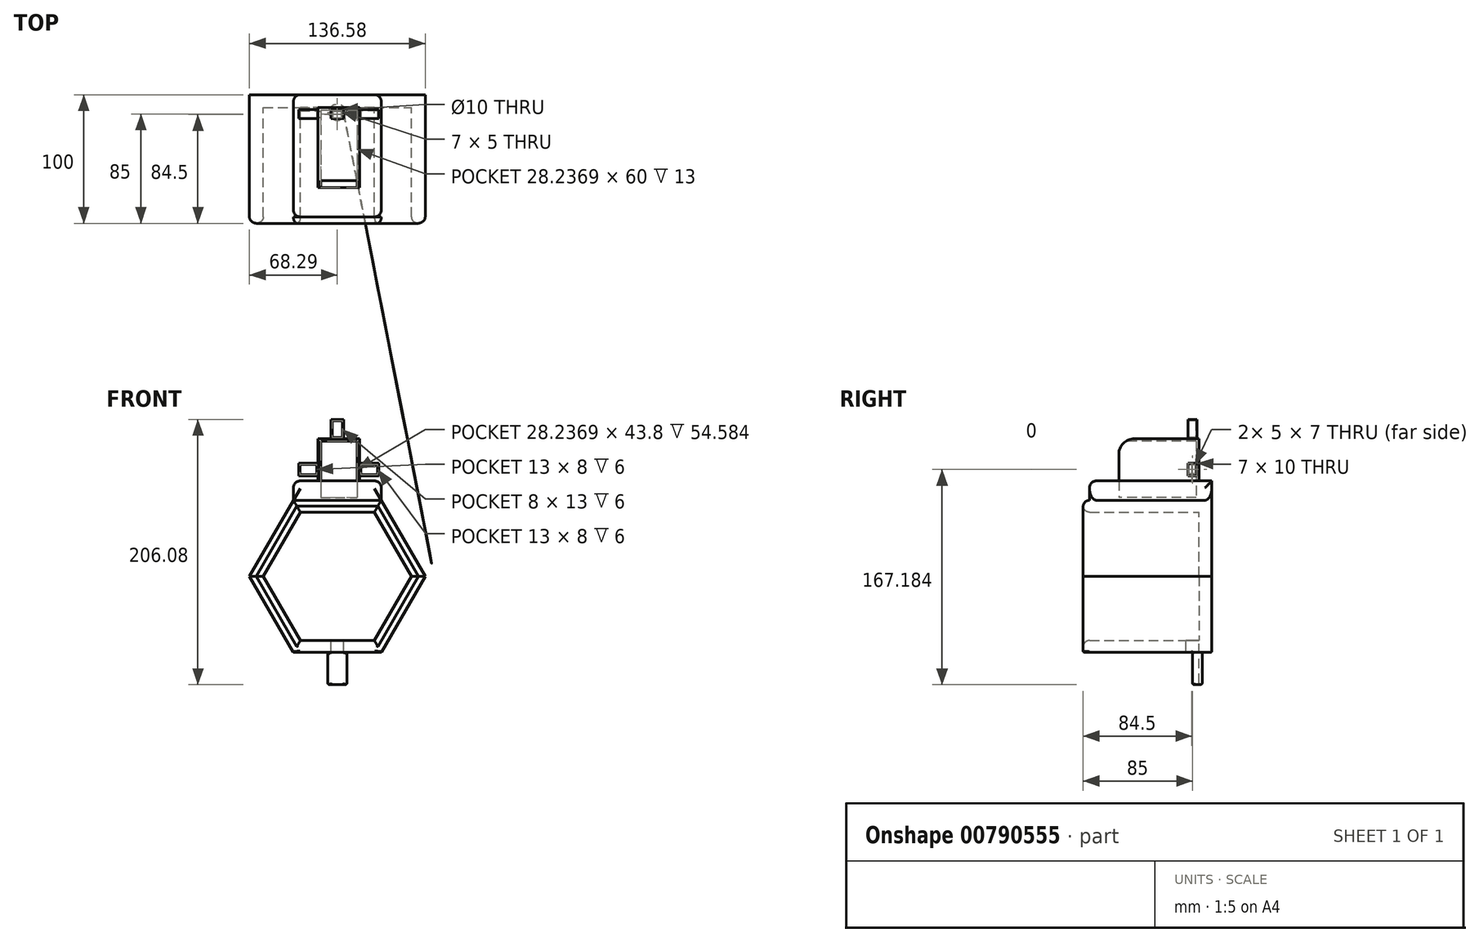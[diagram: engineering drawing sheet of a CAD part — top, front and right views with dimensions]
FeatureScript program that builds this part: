
annotation { "Feature Type Name" : "Feature", "Feature Type Description" : "" }
export const myFeature = defineFeature(function(context is Context, id is Id, definition is map)
    precondition{}
    {
        {
            var Q0;
            Q0=qCreatedBy(makeId("Front.planeOp"),FACE);
            var sketch = newSketch(context, id + "F0", { "sketchPlane" : qUnion([Q0])});
            skLineSegment(sketch, "E0.0", {"start": v(-34.15, 59.14) * mm, "end": v(34.15, 59.14) * mm});
            skLineSegment(sketch, "E0.1", {"start": v(34.15, 59.14) * mm, "end": v(68.3, 0) * mm});
            skLineSegment(sketch, "E0.2", {"start": v(68.3, 0) * mm, "end": v(34.15, -59.14) * mm});
            skLineSegment(sketch, "E0.3", {"start": v(34.15, -59.14) * mm, "end": v(-34.15, -59.14) * mm});
            skLineSegment(sketch, "E0.4", {"start": v(-34.15, -59.14) * mm, "end": v(-68.3, 0) * mm});
            skLineSegment(sketch, "E0.5", {"start": v(-68.3, 0) * mm, "end": v(-34.15, 59.14) * mm});
            skPoint(sketch, "E0.0.midPoint", {"position": v(0, 59.14) * mm});
            skLineSegment(sketch, "E1.0", {"start": v(-28.78, 49.85) * mm, "end": v(28.78, 49.85) * mm});
            skLineSegment(sketch, "E1.1", {"start": v(28.78, 49.85) * mm, "end": v(57.56, 0) * mm});
            skLineSegment(sketch, "E1.2", {"start": v(57.56, 0) * mm, "end": v(28.78, -49.85) * mm});
            skLineSegment(sketch, "E1.3", {"start": v(28.78, -49.85) * mm, "end": v(-28.78, -49.85) * mm});
            skLineSegment(sketch, "E1.4", {"start": v(-28.78, -49.85) * mm, "end": v(-57.56, 0) * mm});
            skLineSegment(sketch, "E1.5", {"start": v(-57.56, 0) * mm, "end": v(-28.78, 49.85) * mm});
            skPoint(sketch, "E1.0.midPoint", {"position": v(0, 49.85) * mm});
            skPoint(sketch, "E1.cCircle.center.orphan", {"position": v(0, 0) * mm});
            skSolve(sketch);
        }
        {
            var Q0;
            Q0=makeQuery(id+"F0.imprint","IMPRINT",FACE,{"disambiguationData":[TD([[makeQuery(id+"F0.imprint","IMPRINT",EDGE,{"derivedFrom":sQuery(id+"F0.wireOp",EDGE,"E0.0")}),-1.0]])]});
            extrude(context, id + "F1", {"entities" : qUnion([Q0]), "depth" : 100 * mm, "offsetDistance" : 25 * mm});
        }
        {
            var Q0;
            Q0=makeQuery(id+"F0.imprint","IMPRINT",FACE,{"disambiguationData":[TD([[makeQuery(id+"F0.imprint","IMPRINT",EDGE,{"derivedFrom":sQuery(id+"F0.wireOp",EDGE,"E1.0")}),-1.0]])]});
            extrude(context, id + "F2", {"entities" : qUnion([Q0]), "operationType" : NewBodyOperationType.ADD, "depth" : 10 * mm, "offsetDistance" : 25 * mm});
        }
        {
            var Q0;
            Q0=makeQuery(id+"F1.opExtrude","SWEPT_FACE",FACE,{"disambiguationData":[OSD([sQuery(id+"F0.wireOp",EDGE,"E0.3")])]});
            var sketch = newSketch(context, id + "F3", { "sketchPlane" : qUnion([Q0])});
            skArc(sketch, "E2", {"start": v(-5, 15) * mm, "mid": v(0, 10) * mm, "end": v(5, 15) * mm});
            skPoint(sketch, "E3.start.orphan", {"position": v(0, 0) * mm});
            skArc(sketch, "E4", {"start": v(-7.5, 15) * mm, "mid": v(0, 7.5) * mm, "end": v(7.5, 15) * mm});
            skPoint(sketch, "E5.orphan", {"position": v(0, 20) * mm});
            skPoint(sketch, "E6.end.orphan", {"position": v(0, 10) * mm});
            skLineSegment(sketch, "E7", {"start": v(-5, 15) * mm, "end": v(-7.5, 15) * mm});
            skLineSegment(sketch, "E8.trimOffspring", {"start": v(5, 15) * mm, "end": v(7.5, 15) * mm});
            skSolve(sketch);
        }
        {
            var Q0;
            Q0=makeQuery(id+"F3.imprint","IMPRINT",FACE,{"disambiguationData":[TD([[makeQuery(id+"F3.imprint","IMPRINT",EDGE,{"derivedFrom":sQuery(id+"F3.wireOp",EDGE,"E2")}),-1.0]])]});
            extrude(context, id + "F4", {"entities" : qUnion([Q0]), "operationType" : NewBodyOperationType.ADD, "depth" : 25 * mm, "offsetDistance" : 25 * mm});
        }
        {
            var Q0;
            Q0=makeQuery(id+"F1.opExtrude","SWEPT_FACE",FACE,{"disambiguationData":[OSD([sQuery(id+"F0.wireOp",EDGE,"E0.3")])]});
            var sketch = newSketch(context, id + "F5", { "sketchPlane" : qUnion([Q0])});
            skCircle(sketch, "E9", {"center": v(0, 15) * mm, "radius": 5 * mm});
            skSolve(sketch);
        }
        {
            var Q0;
            {var subQ0=sQuery(id+"F5.wireOp",EDGE,"E9");var subQ1=makeQuery(id+"F5.imprint","INTERSECT",VERTEX,{"derivedFrom":[makeQuery(id+"F4.opExtrude","CAP_EDGE",EDGE,{"disambiguationData":[OSD([sQuery(id+"F3.wireOp",EDGE,"E7")])],"isStart":true}),subQ0]});Q0=makeQuery(id+"F5.imprint","IMPRINT",FACE,{"disambiguationData":[TD([[makeQuery(id+"F5.imprint","IMPRINT",EDGE,{"disambiguationData":[TD([[subQ1,1.0]])],"derivedFrom":subQ0}),1.0]])]});}
            extrude(context, id + "F6", {"entities" : qUnion([Q0]), "operationType" : NewBodyOperationType.REMOVE, "oppositeDirection" : true, "depth" : 25 * mm, "offsetDistance" : 25 * mm});
        }
        {
            var Q0;
            Q0=makeQuery(id+"F4.opExtrude","CAP_FACE",FACE,{"disambiguationData":[OSD([sQuery(id+"F3.wireOp",EDGE,"E2"),sQuery(id+"F3.wireOp",EDGE,"E4"),sQuery(id+"F3.wireOp",EDGE,"E7"),sQuery(id+"F3.wireOp",EDGE,"E8.trimOffspring")])],"isStart":false});
            fillet(context, id + "F7", {"entities" : qUnion([Q0]), "radius" : 1.13 * mm, "tangentPropagation" : true, "allowEdgeOverflow" : false});
        }
        {
            var Q0;
            Q0=makeQuery(id+"F4.opExtrude","SWEPT_FACE",FACE,{"disambiguationData":[OSD([sQuery(id+"F3.wireOp",EDGE,"E7")])]});
            var Q1;
            Q1=makeQuery(id+"F4.opExtrude","SWEPT_FACE",FACE,{"disambiguationData":[OSD([sQuery(id+"F3.wireOp",EDGE,"E8.trimOffspring")])]});
            var Q2;
            Q2=makeQuery(id+"F1.opExtrude","SWEPT_FACE",FACE,{"disambiguationData":[OSD([sQuery(id+"F0.wireOp",EDGE,"E0.3")])]});
            fillet(context, id + "F8", {"entities" : qUnion([Q0, Q1, Q2]), "radius" : 1.1 * mm, "tangentPropagation" : true, "allowEdgeOverflow" : false});
        }
        {
            var Q0;
            Q0=makeQuery(id+"F1.opExtrude","CAP_FACE",FACE,{"disambiguationData":[OSD([sQuery(id+"F0.wireOp",EDGE,"E0.0"),sQuery(id+"F0.wireOp",EDGE,"E0.1"),sQuery(id+"F0.wireOp",EDGE,"E0.2"),sQuery(id+"F0.wireOp",EDGE,"E0.3"),sQuery(id+"F0.wireOp",EDGE,"E0.4"),sQuery(id+"F0.wireOp",EDGE,"E0.5"),sQuery(id+"F0.wireOp",EDGE,"E1.0"),sQuery(id+"F0.wireOp",EDGE,"E1.1"),sQuery(id+"F0.wireOp",EDGE,"E1.2"),sQuery(id+"F0.wireOp",EDGE,"E1.3"),sQuery(id+"F0.wireOp",EDGE,"E1.4"),sQuery(id+"F0.wireOp",EDGE,"E1.5")])],"isStart":false});
            fillet(context, id + "F9", {"entities" : qUnion([Q0]), "radius" : 5 * mm, "tangentPropagation" : true, "allowEdgeOverflow" : false});
        }
        {
            var Q0;
            Q0=makeQuery(id+"F1.opExtrude","SWEPT_FACE",FACE,{"disambiguationData":[OSD([sQuery(id+"F0.wireOp",EDGE,"E0.0")])]});
            var sketch = newSketch(context, id + "F10", { "sketchPlane" : qUnion([Q0])});
            skLineSegment(sketch, "E10", {"start": v(17.28, -72.27) * mm, "end": v(17.28, -10) * mm});
            skLineSegment(sketch, "E11", {"start": v(17.28, -72.27) * mm, "end": v(-14.96, -72.27) * mm});
            skLineSegment(sketch, "E12", {"start": v(-14.96, -72.27) * mm, "end": v(-14.96, -10) * mm});
            skLineSegment(sketch, "E13", {"start": v(-14.96, -10) * mm, "end": v(17.28, -10) * mm});
            skSolve(sketch);
        }
        {
            var Q0;
            Q0=makeQuery(id+"F10.imprint","IMPRINT",FACE,{"disambiguationData":[TD([[makeQuery(id+"F10.imprint","IMPRINT",EDGE,{"derivedFrom":sQuery(id+"F10.wireOp",EDGE,"E10")}),1.0]])]});
            extrude(context, id + "F11", {"entities" : qUnion([Q0]), "operationType" : NewBodyOperationType.ADD, "depth" : 47.8 * mm, "offsetDistance" : 25 * mm});
        }
        {
            var Q0;
            Q0=makeQuery(id+"F11.opExtrude","SWEPT_FACE",FACE,{"disambiguationData":[OSD([sQuery(id+"F10.wireOp",EDGE,"E11")])]});
            var sketch = newSketch(context, id + "F12", { "sketchPlane" : qUnion([Q0])});
            skLineSegment(sketch, "E14.0", {"start": v(15.28, 104.94) * mm, "end": v(15.28, 61.14) * mm});
            skLineSegment(sketch, "E15.0", {"start": v(-12.96, 61.14) * mm, "end": v(15.28, 61.14) * mm});
            skLineSegment(sketch, "E16.0", {"start": v(-12.96, 104.94) * mm, "end": v(-12.96, 61.14) * mm});
            skLineSegment(sketch, "E17.0", {"start": v(15.28, 104.94) * mm, "end": v(-12.96, 104.94) * mm});
            skSolve(sketch);
        }
        {
            var Q0;
            Q0=makeQuery(id+"F12.imprint","IMPRINT",FACE,{"disambiguationData":[TD([[makeQuery(id+"F12.imprint","IMPRINT",EDGE,{"derivedFrom":sQuery(id+"F12.wireOp",EDGE,"E14.0")}),-1.0]])]});
            extrude(context, id + "F13", {"entities" : qUnion([Q0]), "operationType" : NewBodyOperationType.REMOVE, "oppositeDirection" : true, "depth" : 60 * mm, "offsetDistance" : 25 * mm});
        }
        {
            var Q0;
            Q0=makeQuery(id+"F11.opExtrude","CAP_FACE",FACE,{"disambiguationData":[OSD([sQuery(id+"F10.wireOp",EDGE,"E10"),sQuery(id+"F10.wireOp",EDGE,"E11"),sQuery(id+"F10.wireOp",EDGE,"E12"),sQuery(id+"F10.wireOp",EDGE,"E13")])],"isStart":false});
            var sketch = newSketch(context, id + "F14", { "sketchPlane" : qUnion([Q0])});
            skPoint(sketch, "E18.startSnap0", {"position": v(1.16, -10) * mm});
            skPoint(sketch, "E19.middle", {"position": v(0, -15) * mm});
            skPoint(sketch, "E19.cornerSnap0", {"position": v(0, -12.5) * mm});
            skLineSegment(sketch, "E20.bottom", {"start": v(5, -11.5) * mm, "end": v(-5, -11.5) * mm});
            skLineSegment(sketch, "E20.top", {"start": v(5, -18.5) * mm, "end": v(-5, -18.5) * mm});
            skLineSegment(sketch, "E20.left", {"start": v(5, -11.5) * mm, "end": v(5, -18.5) * mm});
            skLineSegment(sketch, "E20.right", {"start": v(-5, -11.5) * mm, "end": v(-5, -18.5) * mm});
            skPoint(sketch, "E18.start.orphan", {"position": v(0, -10) * mm});
            skSolve(sketch);
        }
        {
            var Q0;
            Q0=makeQuery(id+"F11.opExtrude","SWEPT_FACE",FACE,{"disambiguationData":[OSD([sQuery(id+"F10.wireOp",EDGE,"E12")])]});
            var sketch = newSketch(context, id + "F15", { "sketchPlane" : qUnion([Q0])});
            skLineSegment(sketch, "E21.bottom", {"start": v(18.5, 88.04) * mm, "end": v(11.5, 88.04) * mm});
            skLineSegment(sketch, "E21.top", {"start": v(18.5, 78.04) * mm, "end": v(11.5, 78.04) * mm});
            skLineSegment(sketch, "E21.left", {"start": v(18.5, 88.04) * mm, "end": v(18.5, 78.04) * mm});
            skLineSegment(sketch, "E21.right", {"start": v(11.5, 88.04) * mm, "end": v(11.5, 78.04) * mm});
            skPoint(sketch, "E21.middle", {"position": v(15, 83.04) * mm});
            skPoint(sketch, "E22.start.orphan", {"position": v(10, 83.04) * mm});
            skSolve(sketch);
        }
        {
            var Q0;
            Q0=makeQuery(id+"F11.opExtrude","SWEPT_FACE",FACE,{"disambiguationData":[OSD([sQuery(id+"F10.wireOp",EDGE,"E10")])]});
            var sketch = newSketch(context, id + "F16", { "sketchPlane" : qUnion([Q0])});
            skLineSegment(sketch, "E23.bottom", {"start": v(-11.5, 78.04) * mm, "end": v(-18.5, 78.04) * mm});
            skLineSegment(sketch, "E23.top", {"start": v(-11.5, 88.04) * mm, "end": v(-18.5, 88.04) * mm});
            skLineSegment(sketch, "E23.left", {"start": v(-11.5, 78.04) * mm, "end": v(-11.5, 88.04) * mm});
            skLineSegment(sketch, "E23.right", {"start": v(-18.5, 78.04) * mm, "end": v(-18.5, 88.04) * mm});
            skPoint(sketch, "E23.middle", {"position": v(-15, 83.04) * mm});
            skPoint(sketch, "E24.start.orphan", {"position": v(-10, 83.04) * mm});
            skSolve(sketch);
        }
        {
            var Q0;
            Q0 = qSketchRegion(id + "F14", true);
            var Q1;
            Q1=makeQuery(id+"F1.opExtrude","SWEPT_FACE",FACE,{"disambiguationData":[OSD([sQuery(id+"F0.wireOp",EDGE,"E0.0")])]});
            extrude(context, id + "F17", {"entities" : qUnion([Q0, Q1]), "operationType" : NewBodyOperationType.ADD, "depth" : 15 * mm, "offsetDistance" : 25 * mm});
        }
        {
            var Q0;
            Q0 = qSketchRegion(id + "F15", true);
            extrude(context, id + "F18", {"entities" : qUnion([Q0]), "operationType" : NewBodyOperationType.ADD, "depth" : 15 * mm, "offsetDistance" : 25 * mm});
        }
        {
            var Q0;
            Q0=makeQuery(id+"F16.imprint","IMPRINT",FACE,{"disambiguationData":[TD([[makeQuery(id+"F16.imprint","IMPRINT",EDGE,{"derivedFrom":sQuery(id+"F16.wireOp",EDGE,"E23.bottom")}),-1.0]])]});
            extrude(context, id + "F19", {"entities" : qUnion([Q0]), "operationType" : NewBodyOperationType.ADD, "depth" : 15 * mm, "offsetDistance" : 25 * mm});
        }
        {
            var Q0;
            Q0=makeQuery(id+"F18.opExtrude","SWEPT_FACE",FACE,{"disambiguationData":[OSD([sQuery(id+"F15.wireOp",EDGE,"E21.left")])]});
            var sketch = newSketch(context, id + "F20", { "sketchPlane" : qUnion([Q0])});
            skLineSegment(sketch, "E25.0", {"start": v(-15.96, 87.04) * mm, "end": v(-15.96, 79.04) * mm});
            skLineSegment(sketch, "E26.0", {"start": v(-28.96, 87.04) * mm, "end": v(-15.96, 87.04) * mm});
            skLineSegment(sketch, "E27.0", {"start": v(-28.96, 79.04) * mm, "end": v(-15.96, 79.04) * mm});
            skLineSegment(sketch, "E28.0", {"start": v(-28.96, 87.04) * mm, "end": v(-28.96, 79.04) * mm});
            skSolve(sketch);
        }
        {
            var Q0;
            Q0=makeQuery(id+"F20.imprint","IMPRINT",FACE,{"disambiguationData":[TD([[makeQuery(id+"F20.imprint","IMPRINT",EDGE,{"derivedFrom":sQuery(id+"F20.wireOp",EDGE,"E25.0")}),-1.0]])]});
            extrude(context, id + "F21", {"entities" : qUnion([Q0]), "operationType" : NewBodyOperationType.REMOVE, "oppositeDirection" : true, "depth" : 6 * mm, "offsetDistance" : 25 * mm});
        }
        {
            var Q0;
            Q0=makeQuery(id+"F21.boolean.opBoolean","COPY",FACE,{"derivedFrom":makeQuery(id+"F21.opExtrude","SWEPT_FACE",FACE,{"disambiguationData":[OSD([sQuery(id+"F20.wireOp",EDGE,"E25.0")])]})});
            var sketch = newSketch(context, id + "F22", { "sketchPlane" : qUnion([Q0])});
            skLineSegment(sketch, "E29.0", {"start": v(12.5, 79.54) * mm, "end": v(12.5, 79.54) * mm});
            skLineSegment(sketch, "E30.0", {"start": v(18, 86.54) * mm, "end": v(18, 79.54) * mm});
            skLineSegment(sketch, "E31.0", {"start": v(13, 86.54) * mm, "end": v(18, 86.54) * mm});
            skPoint(sketch, "E32.startSnap0", {"position": v(15.5, 87.04) * mm});
            skLineSegment(sketch, "E33.MirrorCS", {"start": v(13, 86.54) * mm, "end": v(13, 79.54) * mm});
            skLineSegment(sketch, "E34.trimOffspring", {"start": v(13, 79.54) * mm, "end": v(18, 79.54) * mm});
            skSolve(sketch);
        }
        {
            var Q0;
            Q0=makeQuery(id+"F22.imprint","IMPRINT",FACE,{"disambiguationData":[TD([[makeQuery(id+"F22.imprint","IMPRINT",EDGE,{"derivedFrom":sQuery(id+"F22.wireOp",EDGE,"E30.0")}),-1.0]])]});
            extrude(context, id + "F23", {"entities" : qUnion([Q0]), "operationType" : NewBodyOperationType.REMOVE, "oppositeDirection" : true, "depth" : 25 * mm, "offsetDistance" : 25 * mm});
        }
        {
            var Q0;
            Q0=makeQuery(id+"F17.opExtrude","SWEPT_FACE",FACE,{"disambiguationData":[OSD([sQuery(id+"F14.wireOp",EDGE,"E20.top")])]});
            var sketch = newSketch(context, id + "F24", { "sketchPlane" : qUnion([Q0])});
            skLineSegment(sketch, "E35.0", {"start": v(-4, 107.94) * mm, "end": v(4, 107.94) * mm});
            skLineSegment(sketch, "E35.1", {"start": v(-4, 120.94) * mm, "end": v(-4, 107.94) * mm});
            skLineSegment(sketch, "E35.2", {"start": v(4, 120.94) * mm, "end": v(-4, 120.94) * mm});
            skLineSegment(sketch, "E35.3", {"start": v(4, 107.94) * mm, "end": v(4, 120.94) * mm});
            skSolve(sketch);
        }
        {
            var Q0;
            Q0=makeQuery(id+"F24.imprint","IMPRINT",FACE,{"disambiguationData":[TD([[makeQuery(id+"F24.imprint","IMPRINT",EDGE,{"derivedFrom":sQuery(id+"F24.wireOp",EDGE,"E35.0")}),1.0]])]});
            extrude(context, id + "F25", {"entities" : qUnion([Q0]), "operationType" : NewBodyOperationType.REMOVE, "oppositeDirection" : true, "depth" : 6 * mm, "offsetDistance" : 25 * mm});
        }
        {
            var Q0;
            Q0=makeQuery(id+"F25.boolean.opBoolean","COPY",FACE,{"derivedFrom":makeQuery(id+"F25.opExtrude","SWEPT_FACE",FACE,{"disambiguationData":[OSD([sQuery(id+"F24.wireOp",EDGE,"E35.0")])]})});
            var sketch = newSketch(context, id + "F26", { "sketchPlane" : qUnion([Q0])});
            skLineSegment(sketch, "E36.0", {"start": v(-3.5, -18) * mm, "end": v(3.5, -18) * mm});
            skLineSegment(sketch, "E36.1", {"start": v(-3.5, -13) * mm, "end": v(-3.5, -18) * mm});
            skLineSegment(sketch, "E36.2", {"start": v(3.5, -13) * mm, "end": v(-3.5, -13) * mm});
            skLineSegment(sketch, "E36.3", {"start": v(3.5, -18) * mm, "end": v(3.5, -13) * mm});
            skLineSegment(sketch, "E37.0", {"start": v(-9, -23.5) * mm, "end": v(9, -23.5) * mm});
            skLineSegment(sketch, "E37.1", {"start": v(-9, -7.5) * mm, "end": v(-9, -23.5) * mm});
            skLineSegment(sketch, "E37.2", {"start": v(9, -7.5) * mm, "end": v(-9, -7.5) * mm});
            skLineSegment(sketch, "E37.3", {"start": v(9, -23.5) * mm, "end": v(9, -7.5) * mm});
            skSolve(sketch);
        }
        {
            var Q0;
            Q0=makeQuery(id+"F26.imprint","IMPRINT",FACE,{"disambiguationData":[TD([[makeQuery(id+"F26.imprint","IMPRINT",EDGE,{"derivedFrom":sQuery(id+"F26.wireOp",EDGE,"E36.0")}),1.0]])]});
            extrude(context, id + "F27", {"entities" : qUnion([Q0]), "operationType" : NewBodyOperationType.REMOVE, "oppositeDirection" : true, "depth" : 25 * mm, "offsetDistance" : 25 * mm});
        }
        {
            var Q0;
            Q0=makeQuery(id+"F19.opExtrude","SWEPT_FACE",FACE,{"disambiguationData":[OSD([sQuery(id+"F16.wireOp",EDGE,"E23.right")])]});
            var sketch = newSketch(context, id + "F28", { "sketchPlane" : qUnion([Q0])});
            skLineSegment(sketch, "E38.0", {"start": v(18.28, 87.04) * mm, "end": v(18.28, 79.04) * mm});
            skLineSegment(sketch, "E38.1", {"start": v(31.28, 87.04) * mm, "end": v(18.28, 87.04) * mm});
            skLineSegment(sketch, "E38.2", {"start": v(31.28, 79.04) * mm, "end": v(31.28, 87.04) * mm});
            skLineSegment(sketch, "E38.3", {"start": v(18.28, 79.04) * mm, "end": v(31.28, 79.04) * mm});
            skSolve(sketch);
        }
        {
            var Q0;
            Q0=makeQuery(id+"F28.imprint","IMPRINT",FACE,{"disambiguationData":[TD([[makeQuery(id+"F28.imprint","IMPRINT",EDGE,{"derivedFrom":sQuery(id+"F28.wireOp",EDGE,"E38.0")}),1.0]])]});
            extrude(context, id + "F29", {"entities" : qUnion([Q0]), "operationType" : NewBodyOperationType.REMOVE, "oppositeDirection" : true, "depth" : 6 * mm, "offsetDistance" : 25 * mm});
        }
        {
            var Q0;
            Q0=makeQuery(id+"F29.boolean.opBoolean","COPY",FACE,{"derivedFrom":makeQuery(id+"F29.opExtrude","SWEPT_FACE",FACE,{"disambiguationData":[OSD([sQuery(id+"F28.wireOp",EDGE,"E38.0")])]})});
            var sketch = newSketch(context, id + "F30", { "sketchPlane" : qUnion([Q0])});
            skLineSegment(sketch, "E39.0", {"start": v(-18, 86.54) * mm, "end": v(-18, 79.54) * mm});
            skLineSegment(sketch, "E39.1", {"start": v(-13, 86.54) * mm, "end": v(-18, 86.54) * mm});
            skLineSegment(sketch, "E39.2", {"start": v(-13, 79.54) * mm, "end": v(-13, 86.54) * mm});
            skLineSegment(sketch, "E39.3", {"start": v(-18, 79.54) * mm, "end": v(-13, 79.54) * mm});
            skSolve(sketch);
        }
        {
            var Q0;
            Q0=makeQuery(id+"F30.imprint","IMPRINT",FACE,{"disambiguationData":[TD([[makeQuery(id+"F30.imprint","IMPRINT",EDGE,{"derivedFrom":sQuery(id+"F30.wireOp",EDGE,"E39.0")}),1.0]])]});
            extrude(context, id + "F31", {"entities" : qUnion([Q0]), "operationType" : NewBodyOperationType.REMOVE, "oppositeDirection" : true, "depth" : 25 * mm, "offsetDistance" : 25 * mm});
        }
        {
            var Q0;
            {var subQ0=sQuery(id+"F0.wireOp",EDGE,"E0.0");Q0=makeQuery(id+"F17.opExtrude","CAP_EDGE",EDGE,{"disambiguationData":[OSD([subQ0]),TDD([makeQuery(id+"F9.opFillet","BLEND_EDGE",EDGE,{"blendedFrom":[makeQuery(id+"F1.opExtrude","CAP_EDGE",EDGE,{"disambiguationData":[OSD([subQ0])],"isStart":false}),makeQuery(id+"F1.opExtrude","SWEPT_FACE",FACE,{"disambiguationData":[OSD([subQ0])]})],"blendedInto":[makeQuery(id+"F1.opExtrude","SWEPT_FACE",FACE,{"disambiguationData":[OSD([subQ0])]})]})])],"isStart":false});}
            var Q1;
            {var subQ0=sQuery(id+"F0.wireOp",EDGE,"E0.5");var subQ1=sQuery(id+"F0.wireOp",EDGE,"E0.0");Q1=makeQuery(id+"F17.opExtrude","SWEPT_EDGE",EDGE,{"disambiguationData":[OSD([subQ1,subQ0]),TDD([makeQuery(id+"F9.opFillet","BLEND_VERTEX",VERTEX,{"blendedFrom":[makeQuery(id+"F1.opExtrude","CAP_EDGE",EDGE,{"disambiguationData":[OSD([subQ1])],"isStart":false}),makeQuery(id+"F1.opExtrude","CAP_EDGE",EDGE,{"disambiguationData":[OSD([subQ0])],"isStart":false}),makeQuery(id+"F1.opExtrude","SWEPT_FACE",FACE,{"disambiguationData":[OSD([subQ1])]}),makeQuery(id+"F1.opExtrude","SWEPT_FACE",FACE,{"disambiguationData":[OSD([subQ0])]})],"blendedInto":[makeQuery(id+"F1.opExtrude","SWEPT_FACE",FACE,{"disambiguationData":[OSD([subQ1])]}),makeQuery(id+"F1.opExtrude","SWEPT_FACE",FACE,{"disambiguationData":[OSD([subQ0])]})]})])]});}
            var Q2;
            {var subQ0=sQuery(id+"F0.wireOp",EDGE,"E0.1");var subQ1=sQuery(id+"F0.wireOp",EDGE,"E0.0");Q2=makeQuery(id+"F17.opExtrude","SWEPT_EDGE",EDGE,{"disambiguationData":[OSD([subQ1,subQ0]),TDD([makeQuery(id+"F9.opFillet","BLEND_VERTEX",VERTEX,{"blendedFrom":[makeQuery(id+"F1.opExtrude","CAP_EDGE",EDGE,{"disambiguationData":[OSD([subQ1])],"isStart":false}),makeQuery(id+"F1.opExtrude","CAP_EDGE",EDGE,{"disambiguationData":[OSD([subQ0])],"isStart":false}),makeQuery(id+"F1.opExtrude","SWEPT_FACE",FACE,{"disambiguationData":[OSD([subQ1])]}),makeQuery(id+"F1.opExtrude","SWEPT_FACE",FACE,{"disambiguationData":[OSD([subQ0])]})],"blendedInto":[makeQuery(id+"F1.opExtrude","SWEPT_FACE",FACE,{"disambiguationData":[OSD([subQ1])]}),makeQuery(id+"F1.opExtrude","SWEPT_FACE",FACE,{"disambiguationData":[OSD([subQ0])]})]})])]});}
            var Q3;
            Q3=makeQuery(id+"F17.opExtrude","CAP_EDGE",EDGE,{"disambiguationData":[OSD([sQuery(id+"F0.wireOp",EDGE,"E0.0"),sQuery(id+"F0.wireOp",EDGE,"E0.1")])],"isStart":false});
            var Q4;
            {var subQ0=sQuery(id+"F0.wireOp",EDGE,"E0.1");var subQ1=sQuery(id+"F0.wireOp",EDGE,"E0.0");Q4=makeQuery(id+"F17.opExtrude","SWEPT_EDGE",EDGE,{"disambiguationData":[OSD([subQ1,subQ0]),TDD([makeQuery(id+"F1.opExtrude","CAP_VERTEX",VERTEX,{"disambiguationData":[OSD([subQ1,subQ0])],"isStart":true})])]});}
            var Q5;
            Q5=makeQuery(id+"F17.opExtrude","CAP_EDGE",EDGE,{"disambiguationData":[OSD([sQuery(id+"F0.wireOp",EDGE,"E0.0"),sQuery(id+"F0.wireOp",EDGE,"E0.5")])],"isStart":false});
            var Q6;
            {var subQ0=sQuery(id+"F0.wireOp",EDGE,"E0.5");var subQ1=sQuery(id+"F0.wireOp",EDGE,"E0.0");Q6=makeQuery(id+"F17.opExtrude","SWEPT_EDGE",EDGE,{"disambiguationData":[OSD([subQ1,subQ0]),TDD([makeQuery(id+"F1.opExtrude","CAP_VERTEX",VERTEX,{"disambiguationData":[OSD([subQ1,subQ0])],"isStart":true})])]});}
            fillet(context, id + "F32", {"entities" : qUnion([Q0, Q1, Q2, Q3, Q4, Q5, Q6]), "radius" : 5.3 * mm, "tangentPropagation" : true, "allowEdgeOverflow" : false});
        }
        {
            var Q0;
            Q0=makeQuery(id+"F11.opExtrude","CAP_EDGE",EDGE,{"disambiguationData":[OSD([sQuery(id+"F10.wireOp",EDGE,"E11")])],"isStart":false});
            fillet(context, id + "F33", {"entities" : qUnion([Q0]), "radius" : 12.07 * mm, "tangentPropagation" : true, "allowEdgeOverflow" : false});
        }
    });
